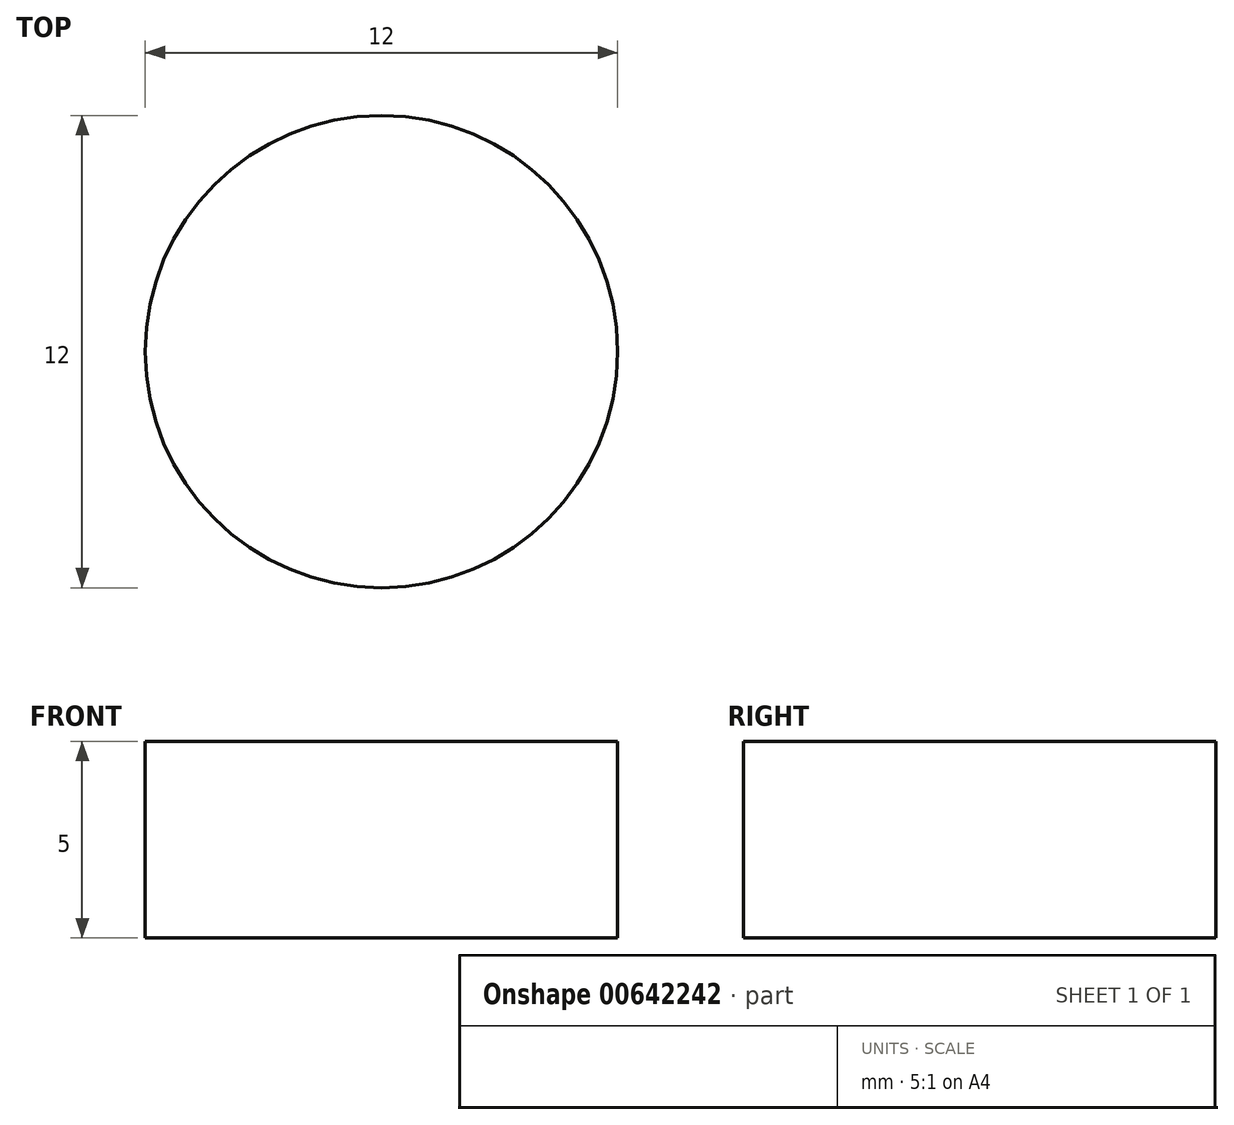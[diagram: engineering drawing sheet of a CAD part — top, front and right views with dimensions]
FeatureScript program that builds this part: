
annotation { "Feature Type Name" : "Feature", "Feature Type Description" : "" }
export const myFeature = defineFeature(function(context is Context, id is Id, definition is map)
    precondition{}
    {
        {
            var Q0;
            Q0=qCreatedBy(makeId("Top.planeOp"),FACE);
            var sketch = newSketch(context, id + "F0", { "sketchPlane" : qUnion([Q0])});
            skCircle(sketch, "E0", {"center": v(0, 0) * mm, "radius": 6 * mm});
            skSolve(sketch);
        }
        {
            var Q0;
            Q0=makeQuery(id+"F0.imprint","IMPRINT",FACE,{"disambiguationData":[TD([[makeQuery(id+"F0.imprint","IMPRINT",EDGE,{"derivedFrom":sQuery(id+"F0.wireOp",EDGE,"E0")}),1.0]])]});
            extrude(context, id + "F1", {"entities" : qUnion([Q0]), "depth" : 5 * mm, "offsetDistance" : 25 * mm});
        }
    });
